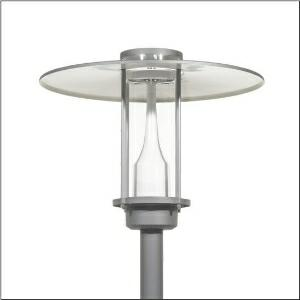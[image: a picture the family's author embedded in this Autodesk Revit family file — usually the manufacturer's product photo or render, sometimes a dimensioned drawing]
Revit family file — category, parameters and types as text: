
# Revit family: city-light_plus_iq___st1_2a_5xa5275kf14h_242a
name_source: partatom
category: Lighting Fixtures
units: mm (PartAtom-declared; Revit-internal decimal feet)

## family parameters
Cut with Voids When Loaded = No
Host = Face
Light Source = No
Part Type = Normal
Room Calculation Point = No
Round Connector Dimension = Use Diameter
Shared = No

## types (1)
- --- (1 x LED, 1470 lm, 10 W, 4000K)
    Apparent Load = 10 VA
    CIE Flux Codes = 22 62 93 97 100
    Color Rendering = 70
    Color Temperature = 4000K
    Default Elevation = 1800 mm
    Description = City-Light Plus iQ, mast luminaire, Module 540 iQ-SR, primary light control with 3 zone facetted reflector, of plastic, silver coated, highly specular, structured, primary optical cover: cover, of PMMA, transparent, light distribution: ST1.2a, light emission: direct distribution, primary light characteristic: asymmetric, installation type: post-top, LED, High Power LED, rated luminous flux: 1.470lm, luminous efficacy: 147lm/W, light colour: 740, colour temperature: 4000K, control gear: iQ Street-Remote, control: pre-setting: logarithmic dimming characteristic, Street-Remote, Auto-Match, Temp-Guard, Lumen-Switch, Night-Set, Smart-Wire, Light-Fading, Desk-Remote (wireless, voltage-free reading and setting of iQ features in the workshop via application-optimized NFC function/RFID function), optimised constant luminous flux control (CLO 2.0), with terminal, 6-pole, max. 2.5mm², mains connection: 230..240V, AC, 50/60Hz, start of lifetime: 10W, end of service life: 10W, reduction: 5W, luminaire housing, upper part, of glass-fibre reinforced polyester, coated, Siteco® metallic grey (DB 702S), diameter: 750mm, height: 590mm, spigot size: d x l = 76 x 70mm (post-top) | with reducer (optional accessory) 60 x 70mm, mounting height: 3..5m, post-top mast mounting element, of diecast aluminium, coated, Siteco® metallic grey (DB 702S), Module 540 iQ-SR, traffic white (RAL 9016), equipment: standard, protection rating (complete): IP65, insulation class (complete): insulation class II (safety insulation), certification: CE, ENEC, VDE, packaging unit: 1 piece

Light Distribution: ST1.2a
    Height = 590 mm
    Lamp = 1 x LED
    Lamp Light Flux = 1470 lm
    Lamp Power = 10 W
    Lamp count = 1
    Length = 750 mm
    Luminous efficacy = 147 lm/W
    Manufacturer = Siteco
    ModVariant = No
    Model = 5XA5275KF14H
    Number of Poles = 1
    OnlyDefault = Yes
    Power Factor = 1
    Product Name = City-Light Plus iQ | ST1.2a
    Product group = mast luminaire | pylon top
    ProductGroupID = 6100
    Protection Class = Protection class II
    Protection Degree = IP 65
    RLX_Detail_Level = 1
    RLX_Emergency_Light_Flux = 0 lm
    RLX_Emergency_Type = 0
    RLX_Emergency_Type_DB = No
    RlxData = <blob elided: 95717 chars, md5=51ccde79>
    Socket = socket
    Standby Power = 0 W
    System Light Flux = 1470 lm
    System Power = 10 W
    Type Comments = factory setting: luminous flux: 100 % | dim-lin: 254 | 401 mA
    Type Image = l_1006456.jpg
    URL = http://relux.com
    VarID = @adj_160108
    Voltage = 0 V
    Weight = 0.00 kg
    Width = 0 mm  [stored 0 ft]

note: [stored X ft] marks values corroborated as IEEE doubles in the binary element streams (Revit-internal decimal feet)

## geometry (parser evidence)
native form markers: Blend x4, Sweep x10
no freeform markers — native parametric forms only
